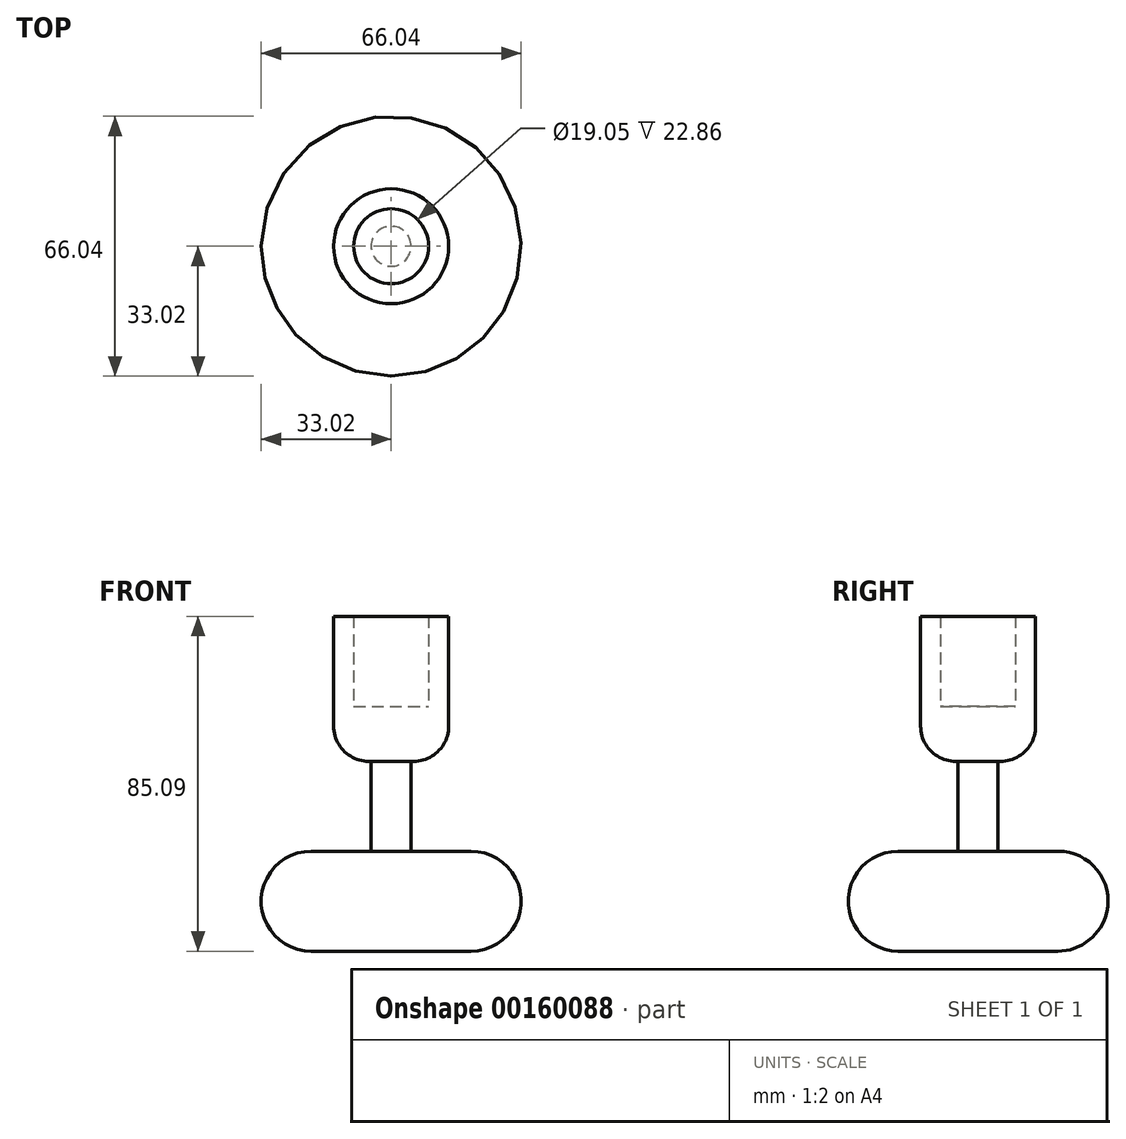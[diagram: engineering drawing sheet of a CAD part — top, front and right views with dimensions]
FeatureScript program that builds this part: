
annotation { "Feature Type Name" : "Feature", "Feature Type Description" : "" }
export const myFeature = defineFeature(function(context is Context, id is Id, definition is map)
    precondition{}
    {
        {
            var Q0;
            Q0=qCreatedBy(makeId("Front.planeOp"),FACE);
            var sketch = newSketch(context, id + "F0", { "sketchPlane" : qUnion([Q0])});
            skLineSegment(sketch, "E0.top", {"start": v(0, -8.9) * mm, "end": v(33.02, -8.9) * mm});
            skLineSegment(sketch, "E0.right", {"start": v(33.02, 16.5) * mm, "end": v(33.02, -8.9) * mm});
            skLineSegment(sketch, "E1.right", {"start": v(14.6, 76.2) * mm, "end": v(14.6, 39.37) * mm});
            skLineSegment(sketch, "E2.right", {"start": v(5.08, 39.37) * mm, "end": v(5.08, 16.5) * mm});
            skLineSegment(sketch, "E3", {"start": v(0, -8.9) * mm, "end": v(0, 76.2) * mm, "construction": true});
            skLineSegment(sketch, "E4.top", {"start": v(0, 53.34) * mm, "end": v(9.52, 53.34) * mm});
            skLineSegment(sketch, "E4.right", {"start": v(9.52, 76.2) * mm, "end": v(9.52, 53.34) * mm});
            skLineSegment(sketch, "E5.trimOffspring", {"start": v(9.52, 76.2) * mm, "end": v(14.6, 76.2) * mm});
            skLineSegment(sketch, "E6.trimOffspring", {"start": v(5.08, 39.37) * mm, "end": v(14.6, 39.37) * mm});
            skLineSegment(sketch, "E7.trimOffspring", {"start": v(5.08, 16.5) * mm, "end": v(33.02, 16.5) * mm});
            skLineSegment(sketch, "E8", {"start": v(0, 53.34) * mm, "end": v(0, -8.9) * mm});
            skSolve(sketch);
        }
        {
            var Q0;
            Q0=makeQuery(id+"F0.imprint","IMPRINT",FACE,{"disambiguationData":[TD([[makeQuery(id+"F0.imprint","IMPRINT",EDGE,{"derivedFrom":sQuery(id+"F0.wireOp",EDGE,"E0.top")}),1.0]])]});
            var Q1;
            Q1=sQuery(id+"F0.wireOp",EDGE,"E3");
            revolve(context, id + "F1", {"entities" : qUnion([Q0]), "axis" : qUnion([Q1]), "revolveType" : RevolveType.FULL});
        }
        {
            var Q0;
            Q0=makeQuery(id+"F1.opRevolve","SWEPT_EDGE",EDGE,{"disambiguationData":[OSD([sQuery(id+"F0.wireOp",EDGE,"E0.right"),sQuery(id+"F0.wireOp",EDGE,"E7.trimOffspring")])]});
            var Q1;
            Q1=makeQuery(id+"F1.opRevolve","SWEPT_EDGE",EDGE,{"disambiguationData":[OSD([sQuery(id+"F0.wireOp",EDGE,"E0.top"),sQuery(id+"F0.wireOp",EDGE,"E0.right")])]});
            fillet(context, id + "F2", {"entities" : qUnion([Q0, Q1]), "radius" : 12.7 * mm, "tangentPropagation" : true, "allowEdgeOverflow" : false});
        }
        {
            var Q0;
            Q0=makeQuery(id+"F1.opRevolve","SWEPT_EDGE",EDGE,{"disambiguationData":[OSD([sQuery(id+"F0.wireOp",EDGE,"E1.right"),sQuery(id+"F0.wireOp",EDGE,"E6.trimOffspring")])]});
            fillet(context, id + "F3", {"entities" : qUnion([Q0]), "radius" : 8.9 * mm, "tangentPropagation" : true, "allowEdgeOverflow" : false});
        }
    });
